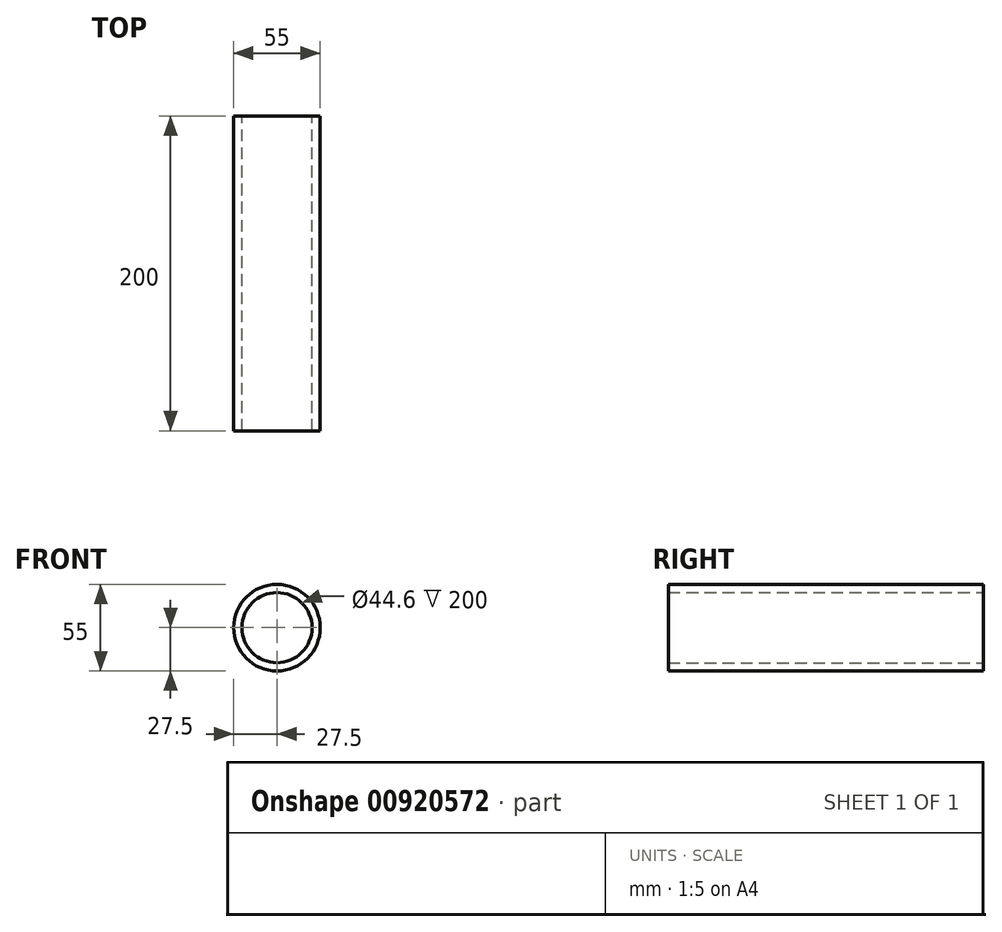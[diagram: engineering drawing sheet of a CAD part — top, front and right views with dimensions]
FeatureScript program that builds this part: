
annotation { "Feature Type Name" : "Feature", "Feature Type Description" : "" }
export const myFeature = defineFeature(function(context is Context, id is Id, definition is map)
    precondition{}
    {
        {
            var Q0;
            Q0=qCreatedBy(makeId("Front.planeOp"),FACE);
            var sketch = newSketch(context, id + "F0", { "sketchPlane" : qUnion([Q0])});
            skCircle(sketch, "E0", {"center": v(0, 0) * mm, "radius": 27.5 * mm});
            skCircle(sketch, "E1", {"center": v(0, 0) * mm, "radius": 22.3 * mm});
            skSolve(sketch);
        }
        {
            var Q0;
            Q0 = qSketchRegion(id + "F0", true);
            extrude(context, id + "F1", {"entities" : qUnion([Q0]), "depth" : 200 * mm, "offsetDistance" : 25 * mm, "symmetric" : true});
        }
    });
